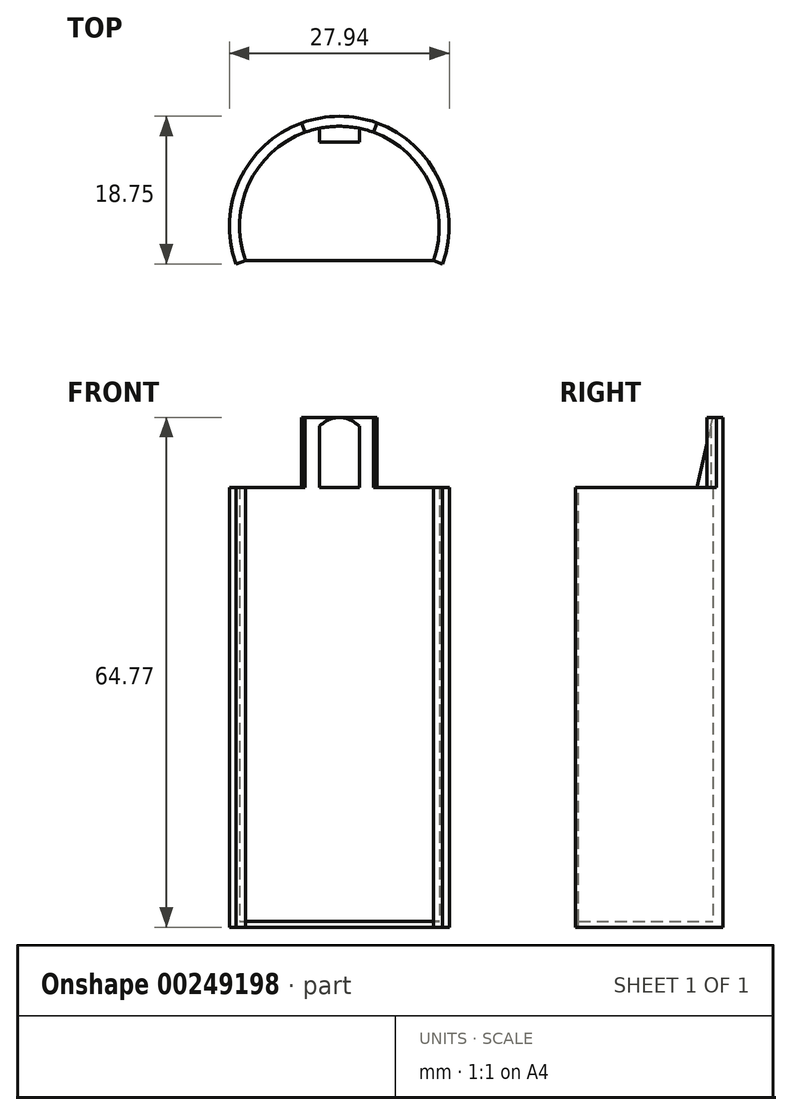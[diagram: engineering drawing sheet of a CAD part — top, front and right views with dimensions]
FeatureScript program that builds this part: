
annotation { "Feature Type Name" : "Feature", "Feature Type Description" : "" }
export const myFeature = defineFeature(function(context is Context, id is Id, definition is map)
    precondition{}
    {
        {
            var Q0;
            Q0=qCreatedBy(makeId("Top.planeOp"),FACE);
            var sketch = newSketch(context, id + "F0", { "sketchPlane" : qUnion([Q0])});
            skCircle(sketch, "E0", {"center": v(0, 0) * mm, "radius": 12.7 * mm});
            skCircle(sketch, "E1", {"center": v(0, 0) * mm, "radius": 13.97 * mm});
            skSolve(sketch);
        }
        {
            var Q0;
            Q0=makeQuery(id+"F0.imprint","IMPRINT",FACE,{"disambiguationData":[TD([[makeQuery(id+"F0.imprint","IMPRINT",EDGE,{"derivedFrom":sQuery(id+"F0.wireOp",EDGE,"E0")}),-1.0]])]});
            var Q1;
            Q1=makeQuery(id+"F0.imprint","IMPRINT",FACE,{"disambiguationData":[TD([[makeQuery(id+"F0.imprint","IMPRINT",EDGE,{"derivedFrom":sQuery(id+"F0.wireOp",EDGE,"E0")}),1.0]])]});
            extrude(context, id + "F1", {"entities" : qUnion([Q0, Q1]), "depth" : .28 * mm + .28 * mm + .2 * mm});
        }
        {
            var Q0;
            Q0 = qSketchRegion(id + "F0", true);
            extrude(context, id + "F2", {"entities" : qUnion([Q0]), "operationType" : NewBodyOperationType.ADD, "depth" : 55.88 * mm});
        }
        {
            var Q0;
            Q0=makeQuery(id+"F2.opExtrude","CAP_FACE",FACE,{"disambiguationData":[OSD([sQuery(id+"F0.wireOp",EDGE,"E0"),sQuery(id+"F0.wireOp",EDGE,"E1")])],"isStart":false});
            var sketch = newSketch(context, id + "F3", { "sketchPlane" : qUnion([Q0])});
            skLineSegment(sketch, "E2", {"start": v(-11.93, -4.34) * mm, "end": v(-13.13, -4.78) * mm});
            skLineSegment(sketch, "E3", {"start": v(11.93, -4.34) * mm, "end": v(13.13, -4.78) * mm});
            skArc(sketch, "E4", {"start": v(-11.93, -4.34) * mm, "mid": v(0, -12.7) * mm, "end": v(11.93, -4.34) * mm});
            skArc(sketch, "E5", {"start": v(-13.13, -4.78) * mm, "mid": v(0, -13.97) * mm, "end": v(13.13, -4.78) * mm});
            skLineSegment(sketch, "E6", {"start": v(0, 0) * mm, "end": v(0, -13.97) * mm, "construction": true});
            skSolve(sketch);
        }
        {
            var Q0;
            Q0=makeQuery(id+"F3.imprint","IMPRINT",FACE,{"disambiguationData":[TD([[makeQuery(id+"F3.imprint","IMPRINT",EDGE,{"derivedFrom":sQuery(id+"F3.wireOp",EDGE,"E2")}),1.0]])]});
            var Q1;
            Q1=makeQuery(id+"F1.opExtrude","CAP_FACE",FACE,{"disambiguationData":[OSD([sQuery(id+"F0.wireOp",EDGE,"E1")])],"isStart":false});
            extrude(context, id + "F4", {"entities" : qUnion([Q0]), "operationType" : NewBodyOperationType.REMOVE, "endBound" : BoundingType.UP_TO_SURFACE, "oppositeDirection" : true, "endBoundEntityFace" : qUnion([Q1]), "depth" : 25.4 * mm});
        }
        {
            var Q0;
            {var subQ0=sQuery(id+"F0.wireOp",EDGE,"E1");Q0=makeQuery(id+"F4.boolean.opBoolean","MERGE",FACE,{"derivedFrom":[makeQuery(id+"F1.opExtrude","CAP_FACE",FACE,{"disambiguationData":[OSD([subQ0])],"isStart":false}),makeQuery(id+"F4.opExtrude","CAP_FACE",FACE,{"disambiguationData":[OSD([subQ0])],"isStart":false})]});}
            var sketch = newSketch(context, id + "F5", { "sketchPlane" : qUnion([Q0])});
            skLineSegment(sketch, "E7", {"start": v(-13.13, -4.78) * mm, "end": v(-11.93, -4.34) * mm});
            skLineSegment(sketch, "E8", {"start": v(-11.93, -4.34) * mm, "end": v(11.93, -4.34) * mm});
            skLineSegment(sketch, "E9", {"start": v(11.93, -4.34) * mm, "end": v(13.13, -4.78) * mm});
            skArc(sketch, "E10", {"start": v(-13.13, -4.78) * mm, "mid": v(0, -13.97) * mm, "end": v(13.13, -4.78) * mm});
            skSolve(sketch);
        }
        {
            var Q0;
            Q0 = qSketchRegion(id + "F5", true);
            extrude(context, id + "F6", {"entities" : qUnion([Q0]), "operationType" : NewBodyOperationType.REMOVE, "endBound" : BoundingType.THROUGH_ALL, "oppositeDirection" : true, "depth" : 25.4 * mm});
        }
        {
            var Q0;
            Q0=makeQuery(id+"F2.opExtrude","CAP_FACE",FACE,{"disambiguationData":[OSD([sQuery(id+"F0.wireOp",EDGE,"E0"),sQuery(id+"F0.wireOp",EDGE,"E1")])],"isStart":false});
            var sketch = newSketch(context, id + "F7", { "sketchPlane" : qUnion([Q0])});
            skLineSegment(sketch, "E11", {"start": v(-4.78, 13.13) * mm, "end": v(0, 0) * mm});
            skLineSegment(sketch, "E12", {"start": v(0, 0) * mm, "end": v(4.78, 13.13) * mm});
            skLineSegment(sketch, "E13", {"start": v(0, 0) * mm, "end": v(0, 13.97) * mm, "construction": true});
            skArc(sketch, "E14", {"start": v(4.78, 13.13) * mm, "mid": v(0, 13.97) * mm, "end": v(-4.78, 13.13) * mm});
            skArc(sketch, "E15", {"start": v(4.34, 11.93) * mm, "mid": v(0, 12.7) * mm, "end": v(-4.34, 11.93) * mm});
            skSolve(sketch);
        }
        {
            var Q0;
            {var subQ0=sQuery(id+"F7.wireOp",EDGE,"E14");Q0=makeQuery(id+"F7.imprint","IMPRINT",FACE,{"disambiguationData":[TD([[makeQuery(id+"F7.imprint","IMPRINT",EDGE,{"derivedFrom":subQ0}),1.0]])]});}
            extrude(context, id + "F8", {"entities" : qUnion([Q0]), "operationType" : NewBodyOperationType.ADD, "depth" : 8.9 * mm});
        }
        {
            var Q0;
            Q0=qCreatedBy(makeId("Right.planeOp"),FACE);
            var sketch = newSketch(context, id + "F9", { "sketchPlane" : qUnion([Q0])});
            skLineSegment(sketch, "E16", {"start": v(12.7, 64.77) * mm, "end": v(10.67, 55.88) * mm});
            skLineSegment(sketch, "E17", {"start": v(10.67, 55.88) * mm, "end": v(12.7, 55.88) * mm});
            skLineSegment(sketch, "E18", {"start": v(12.7, 55.88) * mm, "end": v(12.7, 64.77) * mm});
            skSolve(sketch);
        }
        {
            var Q0;
            Q0 = qSketchRegion(id + "F9", true);
            extrude(context, id + "F10", {"entities" : qUnion([Q0]), "operationType" : NewBodyOperationType.ADD, "depth" : 2.54 * mm, "hasSecondDirection" : true, "secondDirectionOppositeDirection" : true, "secondDirectionDepth" : 2.54 * mm});
        }
    });
